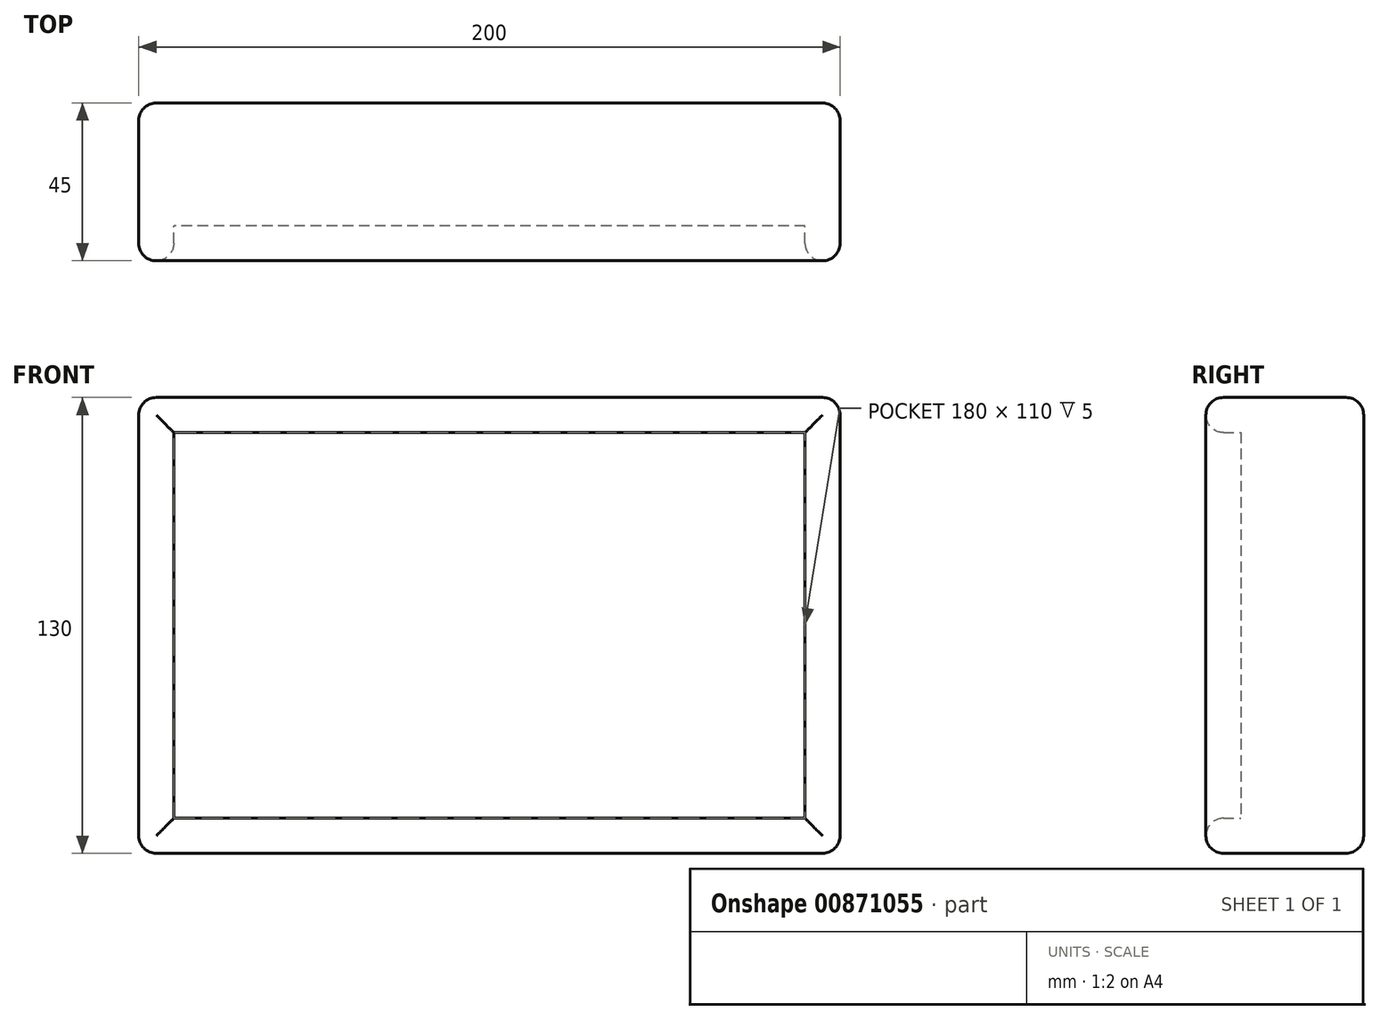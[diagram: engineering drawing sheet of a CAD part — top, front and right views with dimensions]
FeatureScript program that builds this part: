
annotation { "Feature Type Name" : "Feature", "Feature Type Description" : "" }
export const myFeature = defineFeature(function(context is Context, id is Id, definition is map)
    precondition{}
    {
        {
            var Q0;
            Q0=qCreatedBy(makeId("Front.planeOp"),FACE);
            var sketch = newSketch(context, id + "F0", { "sketchPlane" : qUnion([Q0])});
            skLineSegment(sketch, "E0.bottom", {"start": v(90, 55) * mm, "end": v(-90, 55) * mm});
            skLineSegment(sketch, "E0.top", {"start": v(90, -55) * mm, "end": v(-90, -55) * mm});
            skLineSegment(sketch, "E0.left", {"start": v(90, 55) * mm, "end": v(90, -55) * mm});
            skLineSegment(sketch, "E0.right", {"start": v(-90, 55) * mm, "end": v(-90, -55) * mm});
            skPoint(sketch, "E0.middle", {"position": v(0, 0) * mm});
            skLineSegment(sketch, "E1.bottom", {"start": v(100, -65) * mm, "end": v(-100, -65) * mm});
            skLineSegment(sketch, "E1.top", {"start": v(100, 65) * mm, "end": v(-100, 65) * mm});
            skLineSegment(sketch, "E1.left", {"start": v(100, -65) * mm, "end": v(100, 65) * mm});
            skLineSegment(sketch, "E1.right", {"start": v(-100, -65) * mm, "end": v(-100, 65) * mm});
            skSolve(sketch);
        }
        {
            var Q0;
            Q0=makeQuery(id+"F0.imprint","IMPRINT",FACE,{"disambiguationData":[TD([[makeQuery(id+"F0.imprint","IMPRINT",EDGE,{"derivedFrom":sQuery(id+"F0.wireOp",EDGE,"E0.bottom")}),1.0]])]});
            extrude(context, id + "F1", {"entities" : qUnion([Q0]), "depth" : 35 * mm, "offsetDistance" : 25 * mm});
        }
        {
            var Q0;
            Q0=makeQuery(id+"F0.imprint","IMPRINT",FACE,{"disambiguationData":[TD([[makeQuery(id+"F0.imprint","IMPRINT",EDGE,{"derivedFrom":sQuery(id+"F0.wireOp",EDGE,"E0.bottom")}),-1.0]])]});
            extrude(context, id + "F2", {"entities" : qUnion([Q0]), "operationType" : NewBodyOperationType.ADD, "depth" : 45 * mm, "offsetDistance" : 25 * mm});
        }
        {
            var Q0;
            Q0=makeQuery(id+"F2.opExtrude","CAP_FACE",FACE,{"disambiguationData":[OSD([sQuery(id+"F0.wireOp",EDGE,"E0.bottom"),sQuery(id+"F0.wireOp",EDGE,"E0.top"),sQuery(id+"F0.wireOp",EDGE,"E0.left"),sQuery(id+"F0.wireOp",EDGE,"E0.right"),sQuery(id+"F0.wireOp",EDGE,"E1.bottom"),sQuery(id+"F0.wireOp",EDGE,"E1.top"),sQuery(id+"F0.wireOp",EDGE,"E1.left"),sQuery(id+"F0.wireOp",EDGE,"E1.right")])],"isStart":false});
            var Q1;
            Q1=makeQuery(id+"F2.opExtrude","SWEPT_FACE",FACE,{"disambiguationData":[OSD([sQuery(id+"F0.wireOp",EDGE,"E1.bottom")])]});
            var Q2;
            Q2=makeQuery(id+"F2.opExtrude","SWEPT_FACE",FACE,{"disambiguationData":[OSD([sQuery(id+"F0.wireOp",EDGE,"E1.right")])]});
            var Q3;
            Q3=makeQuery(id+"F2.opExtrude","SWEPT_FACE",FACE,{"disambiguationData":[OSD([sQuery(id+"F0.wireOp",EDGE,"E1.left")])]});
            var Q4;
            Q4=makeQuery(id+"F2.opExtrude","SWEPT_FACE",FACE,{"disambiguationData":[OSD([sQuery(id+"F0.wireOp",EDGE,"E1.top")])]});
            fillet(context, id + "F3", {"entities" : qUnion([Q0, Q1, Q2, Q3, Q4]), "radius" : 5 * mm, "tangentPropagation" : true, "allowEdgeOverflow" : false});
        }
    });
